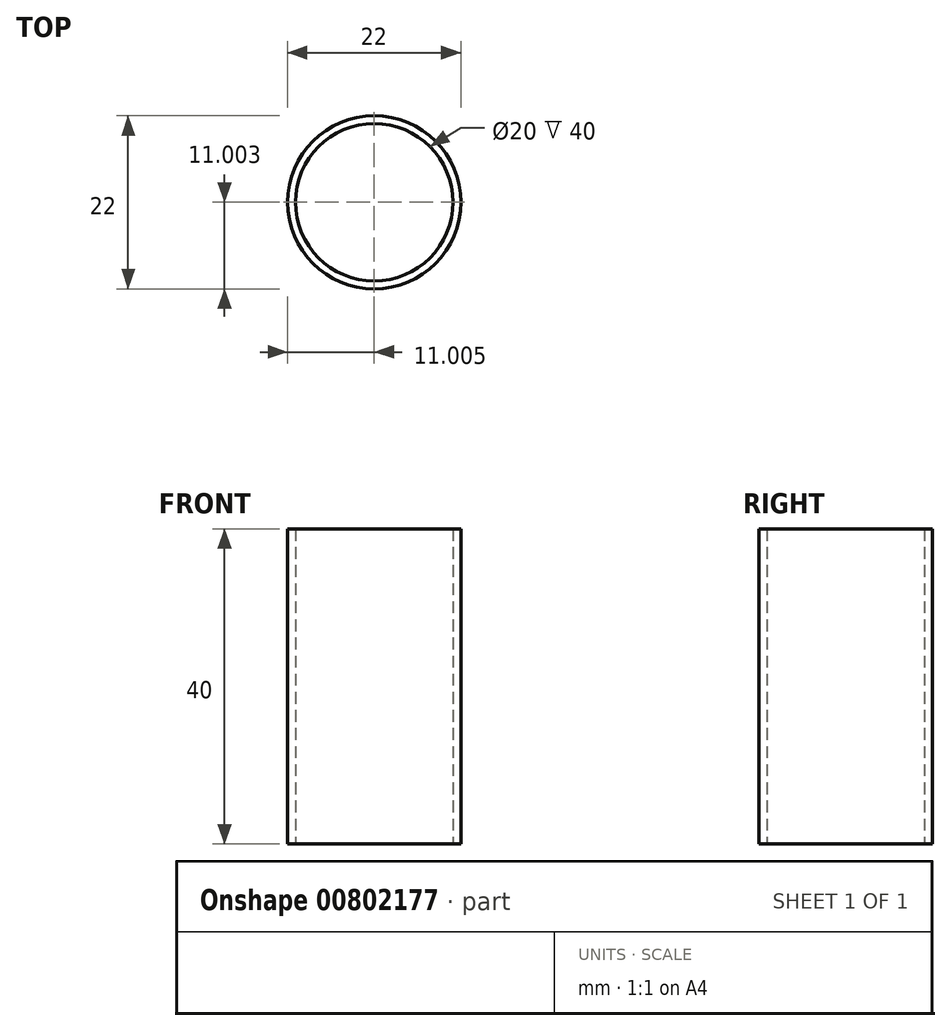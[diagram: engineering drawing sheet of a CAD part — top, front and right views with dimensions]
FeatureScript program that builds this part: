
annotation { "Feature Type Name" : "Feature", "Feature Type Description" : "" }
export const myFeature = defineFeature(function(context is Context, id is Id, definition is map)
    precondition{}
    {
        {
            var Q0;
            Q0=qCreatedBy(makeId("Top.planeOp"),FACE);
            var sketch = newSketch(context, id + "F0", { "sketchPlane" : qUnion([Q0])});
            skCircle(sketch, "E0", {"center": v(-41.1, 32.56) * mm, "radius": 10 * mm});
            skCircle(sketch, "E1", {"center": v(-41.1, 32.56) * mm, "radius": 11 * mm});
            skSolve(sketch);
        }
        {
            var Q0;
            Q0=makeQuery(id+"F0.imprint","IMPRINT",FACE,{"disambiguationData":[TD([[makeQuery(id+"F0.imprint","IMPRINT",EDGE,{"derivedFrom":sQuery(id+"F0.wireOp",EDGE,"E0")}),-1.0]])]});
            extrude(context, id + "F1", {"entities" : qUnion([Q0]), "depth" : 40 * mm, "offsetDistance" : 25 * mm});
        }
    });
